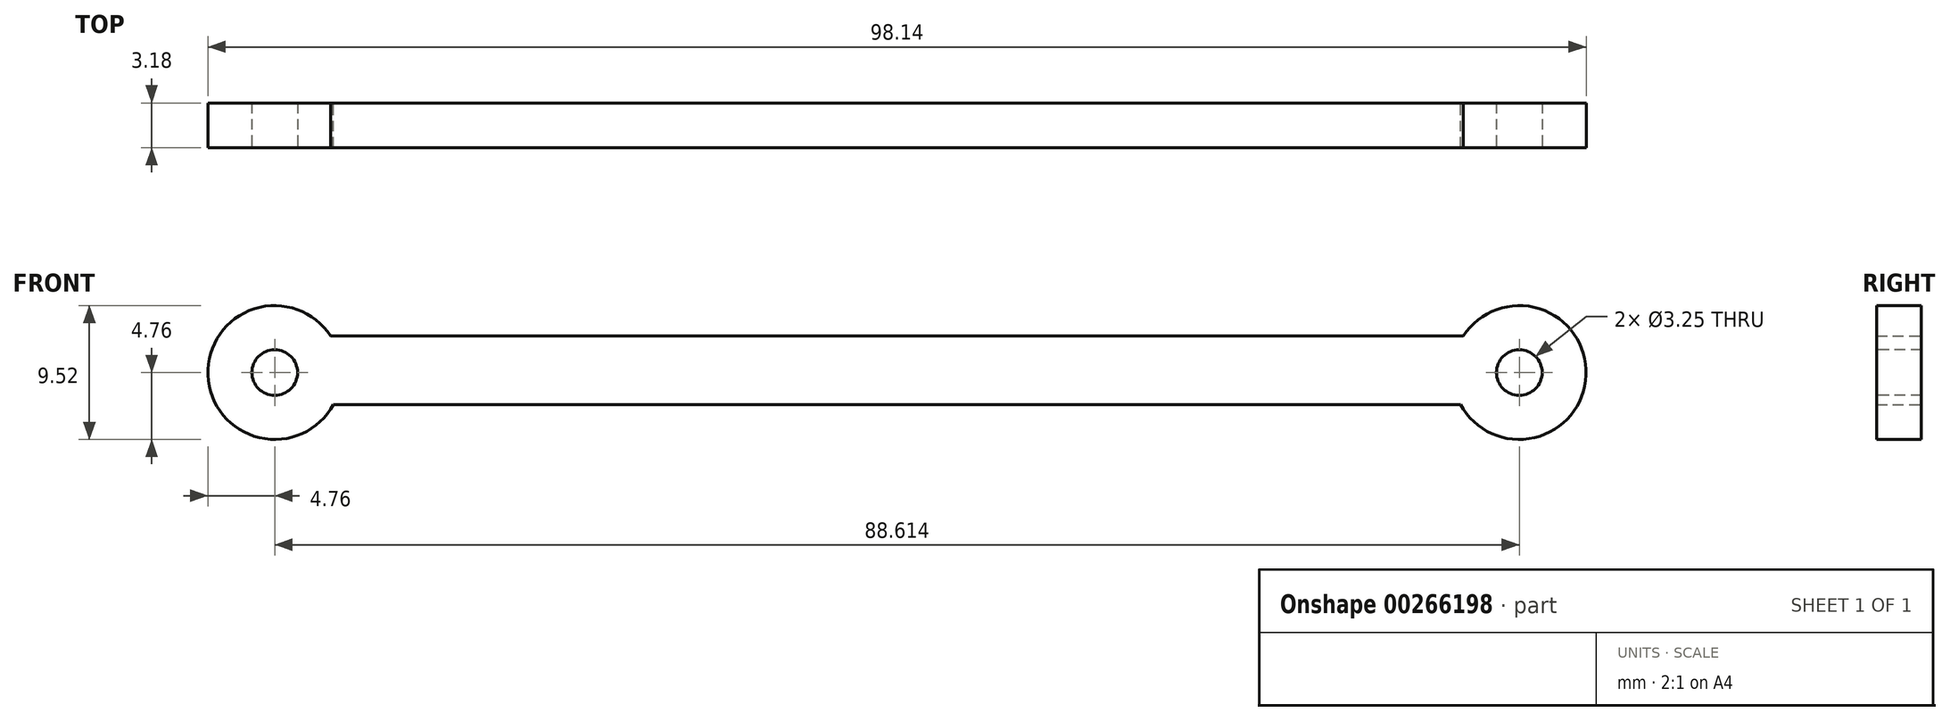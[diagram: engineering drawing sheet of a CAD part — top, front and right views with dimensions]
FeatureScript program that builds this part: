
annotation { "Feature Type Name" : "Feature", "Feature Type Description" : "" }
export const myFeature = defineFeature(function(context is Context, id is Id, definition is map)
    precondition{}
    {
        {
            var Q0;
            Q0=qCreatedBy(makeId("Front.planeOp"),FACE);
            var sketch = newSketch(context, id + "F0", { "sketchPlane" : qUnion([Q0])});
            skCircle(sketch, "E0", {"center": v(0, 0) * mm, "radius": 4.76 * mm});
            skLineSegment(sketch, "E1", {"start": v(0, 2.6) * mm, "end": v(88.9, 2.6) * mm});
            skLineSegment(sketch, "E2", {"start": v(0, -2.27) * mm, "end": v(88.9, -2.27) * mm});
            skCircle(sketch, "E3", {"center": v(88.61, 0) * mm, "radius": 4.76 * mm});
            skSolve(sketch);
        }
        {
            var Q0;
            {var subQ0=sQuery(id+"F0.wireOp",EDGE,"E0");var subQ1=makeQuery(id+"F0.imprint","INTERSECT",VERTEX,{"derivedFrom":[subQ0,sQuery(id+"F0.wireOp",EDGE,"E1")]});Q0=makeQuery(id+"F0.imprint","IMPRINT",FACE,{"disambiguationData":[TD([[makeQuery(id+"F0.imprint","IMPRINT",EDGE,{"disambiguationData":[TD([[subQ1,-1.0]])],"derivedFrom":subQ0}),1.0]])]});}
            var Q1;
            {var subQ0=sQuery(id+"F0.wireOp",EDGE,"E1");var subQ1=sQuery(id+"F0.wireOp",EDGE,"E0");var subQ2=makeQuery(id+"F0.imprint","INTERSECT",VERTEX,{"derivedFrom":[subQ1,subQ0]});Q1=makeQuery(id+"F0.imprint","IMPRINT",FACE,{"disambiguationData":[TD([[makeQuery(id+"F0.imprint","IMPRINT",EDGE,{"disambiguationData":[TD([[subQ2,1.0]])],"derivedFrom":subQ1}),-1.0]])]});}
            var Q2;
            {var subQ0=sQuery(id+"F0.wireOp",EDGE,"E3");var subQ1=makeQuery(id+"F0.imprint","INTERSECT",VERTEX,{"derivedFrom":[sQuery(id+"F0.wireOp",EDGE,"E1"),subQ0]});Q2=makeQuery(id+"F0.imprint","IMPRINT",FACE,{"disambiguationData":[TD([[makeQuery(id+"F0.imprint","IMPRINT",EDGE,{"disambiguationData":[TD([[subQ1,-1.0]])],"derivedFrom":subQ0}),1.0]])]});}
            extrude(context, id + "F1", {"entities" : qUnion([Q0, Q1, Q2]), "depth" : 3.17 * mm});
        }
        {
            var Q0;
            Q0=makeQuery(id+"F1.opExtrude","CAP_FACE",FACE,{"disambiguationData":[OSD([sQuery(id+"F0.wireOp",EDGE,"E0"),sQuery(id+"F0.wireOp",EDGE,"E1"),sQuery(id+"F0.wireOp",EDGE,"E2"),sQuery(id+"F0.wireOp",EDGE,"E3")])],"isStart":false});
            var sketch = newSketch(context, id + "F2", { "sketchPlane" : qUnion([Q0])});
            skCircle(sketch, "E4", {"center": v(0, 0) * mm, "radius": 1.63 * mm});
            skCircle(sketch, "E5", {"center": v(88.61, 0) * mm, "radius": 1.63 * mm});
            skSolve(sketch);
        }
        {
            var Q0;
            Q0=makeQuery(id+"F2.imprint","IMPRINT",FACE,{"disambiguationData":[TD([[makeQuery(id+"F2.imprint","IMPRINT",EDGE,{"derivedFrom":sQuery(id+"F2.wireOp",EDGE,"E4")}),1.0]])]});
            var Q1;
            Q1=makeQuery(id+"F2.imprint","IMPRINT",FACE,{"disambiguationData":[TD([[makeQuery(id+"F2.imprint","IMPRINT",EDGE,{"derivedFrom":sQuery(id+"F2.wireOp",EDGE,"E5")}),1.0]])]});
            extrude(context, id + "F3", {"entities" : qUnion([Q0, Q1]), "operationType" : NewBodyOperationType.REMOVE, "oppositeDirection" : true, "depth" : 25.4 * mm});
        }
    });
